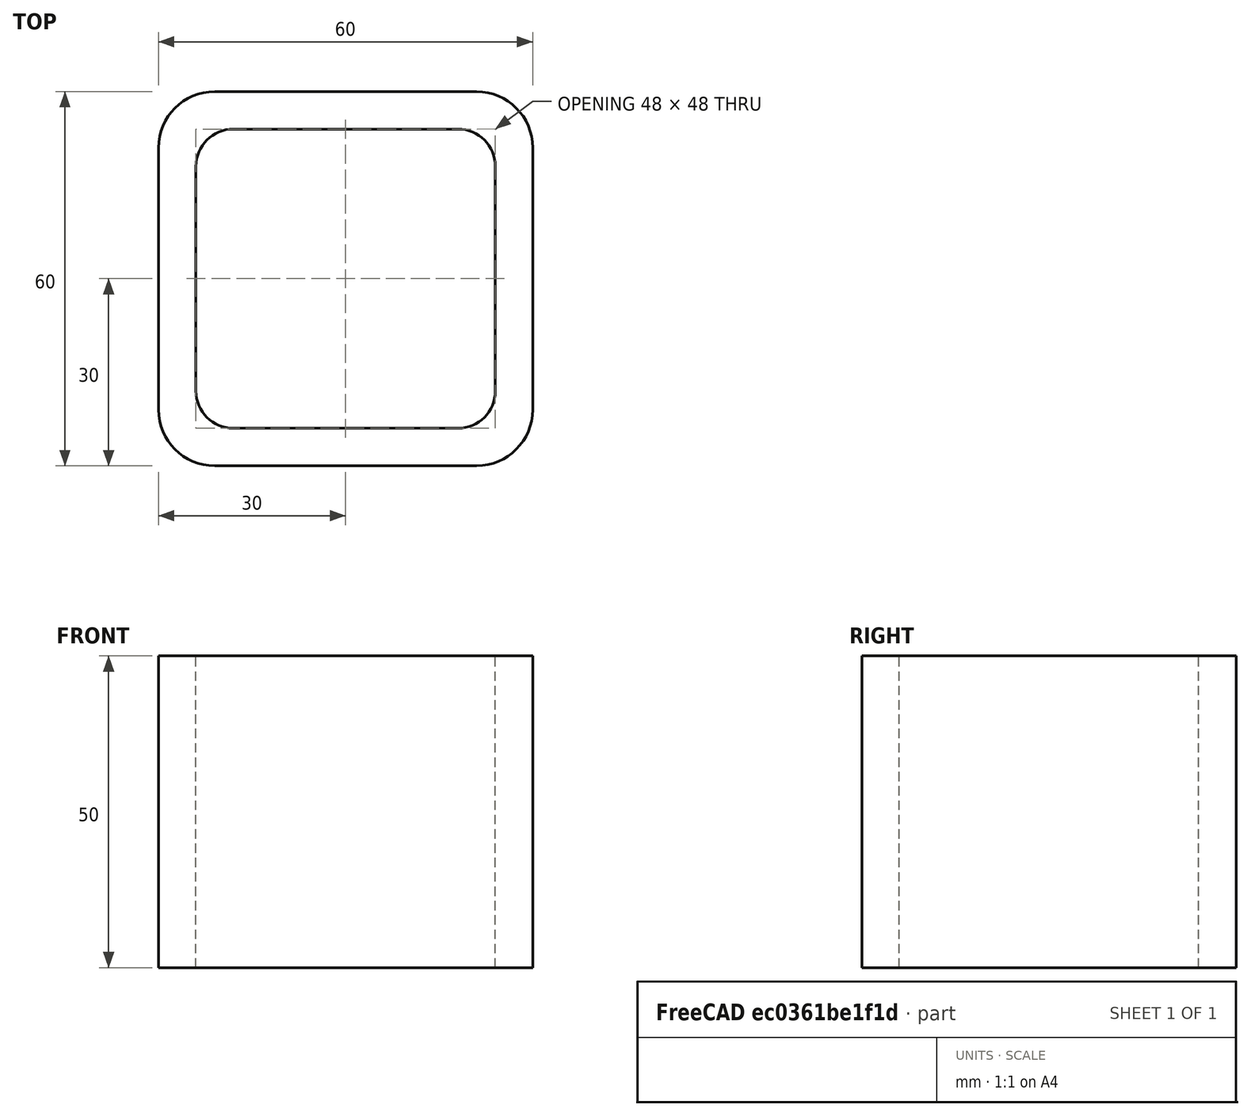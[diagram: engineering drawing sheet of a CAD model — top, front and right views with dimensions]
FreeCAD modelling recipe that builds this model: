
FCSTD DOCUMENT  (FreeCAD 0.15R4671 (Git))
Label: Square hollow section 60x60x6 EN10219 S235JRH
License: All rights reserved
LicenseURL: http://en.wikipedia.org/wiki/All_rights_reserved
objects: Sketcher::SketchObject×1, Part::Extrusion×1
note: 2 computed .brp shape members not serialized (recipe doc carries the construction recipe); baked Part::Feature solids carry a one-line shape summary decoded from their .brp

FEATURE [Sketcher::SketchObject] Sketch
  sketch-geometry (16):
    g0: LineSegment StartX=-18 StartY=24 StartZ=0 EndX=18 EndY=24 EndZ=0
    g1: LineSegment StartX=24 StartY=18 StartZ=0 EndX=24 EndY=-18 EndZ=0
    g2: LineSegment StartX=18 StartY=-24 StartZ=0 EndX=-18 EndY=-24 EndZ=0
    g3: LineSegment StartX=-24 StartY=-18 StartZ=0 EndX=-24 EndY=18 EndZ=0
    g4: LineSegment StartX=-21 StartY=30 StartZ=0 EndX=21 EndY=30 EndZ=0
    g5: LineSegment StartX=30 StartY=21 StartZ=0 EndX=30 EndY=-21 EndZ=0
    g6: LineSegment StartX=21 StartY=-30 StartZ=0 EndX=-21 EndY=-30 EndZ=0
    g7: LineSegment StartX=-30 StartY=-21 StartZ=0 EndX=-30 EndY=21 EndZ=0
    g8: ArcOfCircle CenterX=-18 CenterY=18 CenterZ=0 NormalX=0 NormalY=0 NormalZ=1 Radius=6 StartAngle=1.5708 EndAngle=3.14159
    g9: ArcOfCircle CenterX=18 CenterY=18 CenterZ=0 NormalX=0 NormalY=0 NormalZ=1 Radius=6 StartAngle=0 EndAngle=1.5708
    g10: ArcOfCircle CenterX=18 CenterY=-18 CenterZ=0 NormalX=0 NormalY=0 NormalZ=1 Radius=6 StartAngle=4.71239 EndAngle=6.28319
    g11: ArcOfCircle CenterX=-18 CenterY=-18 CenterZ=0 NormalX=0 NormalY=0 NormalZ=1 Radius=6 StartAngle=3.14159 EndAngle=4.71239
    g12: ArcOfCircle CenterX=21 CenterY=21 CenterZ=0 NormalX=0 NormalY=0 NormalZ=1 Radius=9 StartAngle=0 EndAngle=1.5708
    g13: ArcOfCircle CenterX=21 CenterY=-21 CenterZ=0 NormalX=0 NormalY=0 NormalZ=1 Radius=9 StartAngle=4.71239 EndAngle=6.28319
    g14: ArcOfCircle CenterX=-21 CenterY=-21 CenterZ=0 NormalX=0 NormalY=0 NormalZ=1 Radius=9 StartAngle=3.14159 EndAngle=4.71239
    g15: ArcOfCircle CenterX=-21 CenterY=21 CenterZ=0 NormalX=0 NormalY=0 NormalZ=1 Radius=9 StartAngle=1.5708 EndAngle=3.14159
  constraints (36):
    c: Horizontal(g2)
    c: Vertical(g3)
    c: Horizontal(g6)
    c: Vertical(g7)
    c: Tangent(g3,g8) = 1.5708
    c: Tangent(g0,g8) = 1.5708
    c: Tangent(g0,g9) = 1.5708
    c: Tangent(g1,g9) = 1.5708
    c: Tangent(g1,g10) = 1.5708
    c: Tangent(g2,g10) = 1.5708
    c: Tangent(g2,g11) = 1.5708
    c: Tangent(g3,g11) = 1.5708
    c: Tangent(g4,g12) = 1.5708
    c: Tangent(g5,g12) = 1.5708
    c: Tangent(g5,g13) = 1.5708
    c: Tangent(g6,g13) = 1.5708
    c: Tangent(g6,g14) = 1.5708
    c: Tangent(g7,g14) = 1.5708
    c: Tangent(g7,g15) = 1.5708
    c: Tangent(g4,g15) = 1.5708
    c: Equal(g9,g8)
    c: Equal(g9,g11)
    c: Equal(g9,g10)
    c: Equal(g12,g15)
    c: Equal(g12,g14)
    c: Equal(g12,g13)
    c: Symmetric(g4,g6,g-1)
    c: Symmetric(g7,g5,g-2)
    c: DistanceY(g4,g6) = -60
    c: DistanceX(g7,g5) = 60
    c: Symmetric(g3,g1,g-2)
    c: Symmetric(g0,g2,g-1)
    c: DistanceY(g0,g4) = 6
    c: DistanceX(g5,g1) = -6
    c: Radius(g9) = 6
    c: Radius(g12) = 9
FEATURE [Part::Extrusion] Extrude  label="Square hollow section 60x60x6 EN10219 S235JRH"
  Base = -> Sketch
  Dir = (0,0,50)
  Solid = true
